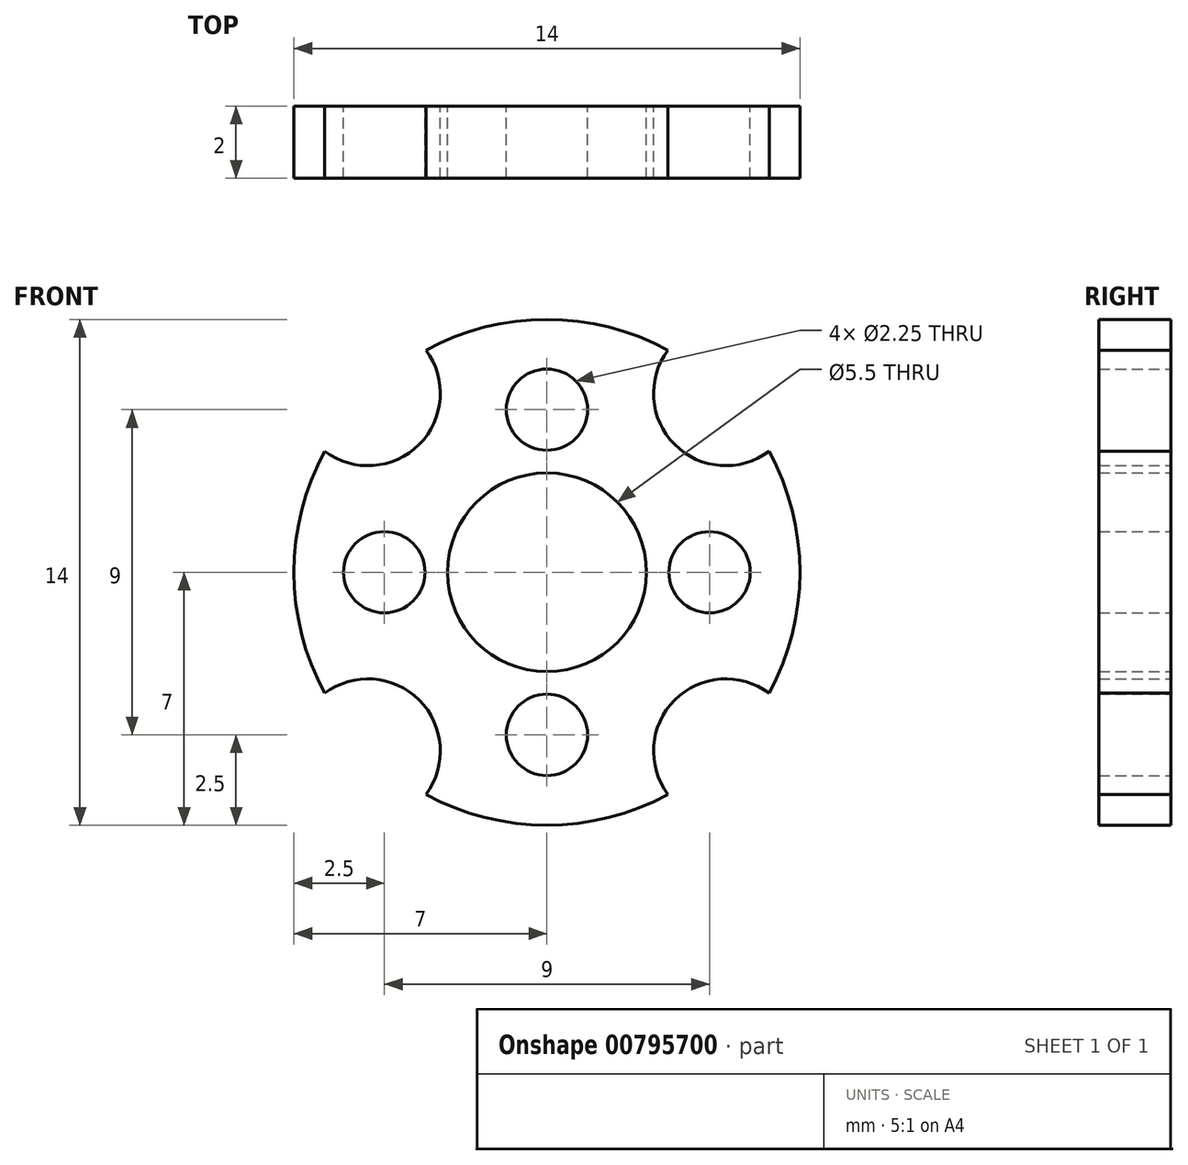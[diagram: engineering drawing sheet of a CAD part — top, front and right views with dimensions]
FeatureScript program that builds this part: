
annotation { "Feature Type Name" : "Feature", "Feature Type Description" : "" }
export const myFeature = defineFeature(function(context is Context, id is Id, definition is map)
    precondition{}
    {
        {
            var Q0;
            Q0=qCreatedBy(makeId("Front.planeOp"),FACE);
            var sketch = newSketch(context, id + "F0", { "sketchPlane" : qUnion([Q0])});
            skLineSegment(sketch, "E0", {"start": v(0, 2.62) * mm, "end": v(0, 7) * mm, "construction": true});
            skCircle(sketch, "E1", {"center": v(0, 4.5) * mm, "radius": 1.13 * mm});
            skCircle(sketch, "E2.1.0", {"center": v(-4.5, 0) * mm, "radius": 1.13 * mm});
            skCircle(sketch, "E2.2.0", {"center": v(0, -4.5) * mm, "radius": 1.13 * mm});
            skPoint(sketch, "E2.center", {"position": v(0, 0) * mm});
            skCircle(sketch, "E3.1.3.0", {"center": v(4.5, 0) * mm, "radius": 1.13 * mm});
            skPoint(sketch, "E4.orphan", {"position": v(-3.43, -3.75) * mm});
            skPoint(sketch, "E5.orphan", {"position": v(3.75, -3.43) * mm});
            skCircle(sketch, "E6", {"center": v(0, 0) * mm, "radius": 2.75 * mm});
            skArc(sketch, "E7", {"start": v(-3.35, -6.15) * mm, "mid": v(0, -7) * mm, "end": v(3.35, -6.15) * mm});
            skLineSegment(sketch, "E8", {"start": v(0, 0) * mm, "end": v(-4.95, 4.95) * mm, "construction": true});
            skLineSegment(sketch, "E9", {"start": v(0, 0) * mm, "end": v(-14.6, 0) * mm, "construction": true});
            skArc(sketch, "E10", {"start": v(-6.15, 3.35) * mm, "mid": v(-3.54, 3.54) * mm, "end": v(-3.35, 6.15) * mm});
            skLineSegment(sketch, "E11", {"start": v(0, 0) * mm, "end": v(4.95, 4.95) * mm, "construction": true});
            skLineSegment(sketch, "E12", {"start": v(0, 0) * mm, "end": v(4.95, -4.95) * mm, "construction": true});
            skLineSegment(sketch, "E13", {"start": v(0, 0) * mm, "end": v(-4.95, -4.95) * mm, "construction": true});
            skArc(sketch, "E14", {"start": v(3.35, 6.15) * mm, "mid": v(3.54, 3.54) * mm, "end": v(6.15, 3.35) * mm});
            skArc(sketch, "E15", {"start": v(6.15, -3.35) * mm, "mid": v(3.54, -3.54) * mm, "end": v(3.35, -6.15) * mm});
            skArc(sketch, "E16", {"start": v(-3.35, -6.15) * mm, "mid": v(-3.54, -3.54) * mm, "end": v(-6.15, -3.35) * mm});
            skArc(sketch, "E17.trimOffspring", {"start": v(-6.15, 3.35) * mm, "mid": v(-7, 0) * mm, "end": v(-6.15, -3.35) * mm});
            skArc(sketch, "E18.trimOffspring", {"start": v(3.35, 6.15) * mm, "mid": v(0, 7) * mm, "end": v(-3.35, 6.15) * mm});
            skArc(sketch, "E19.trimOffspring", {"start": v(6.15, -3.35) * mm, "mid": v(7, 0) * mm, "end": v(6.15, 3.35) * mm});
            skSolve(sketch);
        }
        {
            var Q0;
            Q0 = qSketchRegion(id + "F0", true);
            extrude(context, id + "F1", {"entities" : qUnion([Q0]), "depth" : 2 * mm, "offsetDistance" : 25.4 * mm});
        }
    });
